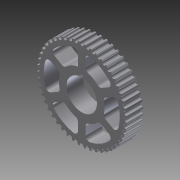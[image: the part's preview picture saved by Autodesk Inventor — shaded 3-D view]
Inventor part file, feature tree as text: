
AUTODESK INVENTOR PART (.ipt)
format: ipt  version: 2012 (Build 160160000, 160)  size: 599,040 bytes
history: native  units: in
note: dims shown in document units (in); Inventor stores cm internally (conversion verified against a paired STEP export)
features: extrude x3, sketch x2, fillet x1, imported_body x1
ambient origin geometry x8: Origin, YZ Plane, XZ Plane, XY Plane, X Axis, Y Axis, Z Axis, Center Point
feature tree (7):
  sketch  "Sketch1"  dims[d0=1.0in d1=1.0in d2=0.0in]
  extrude  "Extrusion1"  Depth=1.0in TaperAngle=0.0deg
  extrude  "Extrusion2"  Depth=0.125in
  extrude  "Extrusion3"  Depth=0.125in
  fillet  "Fillet1"  Radius=0.0625in
  imported_body  "Base1"
  sketch  "Sketch2"  dims[d3=0.3925in d4=0.0in d5=0.125in d6=0.125in d7=0.0625in d8=0.4375in d9=1.25in d10=0.75in d11=60.0deg d12=0.125in d13=0.125in d14=2.3622in d16=360.0deg d18=1.0in d19=0.0in d20=0.125in]
